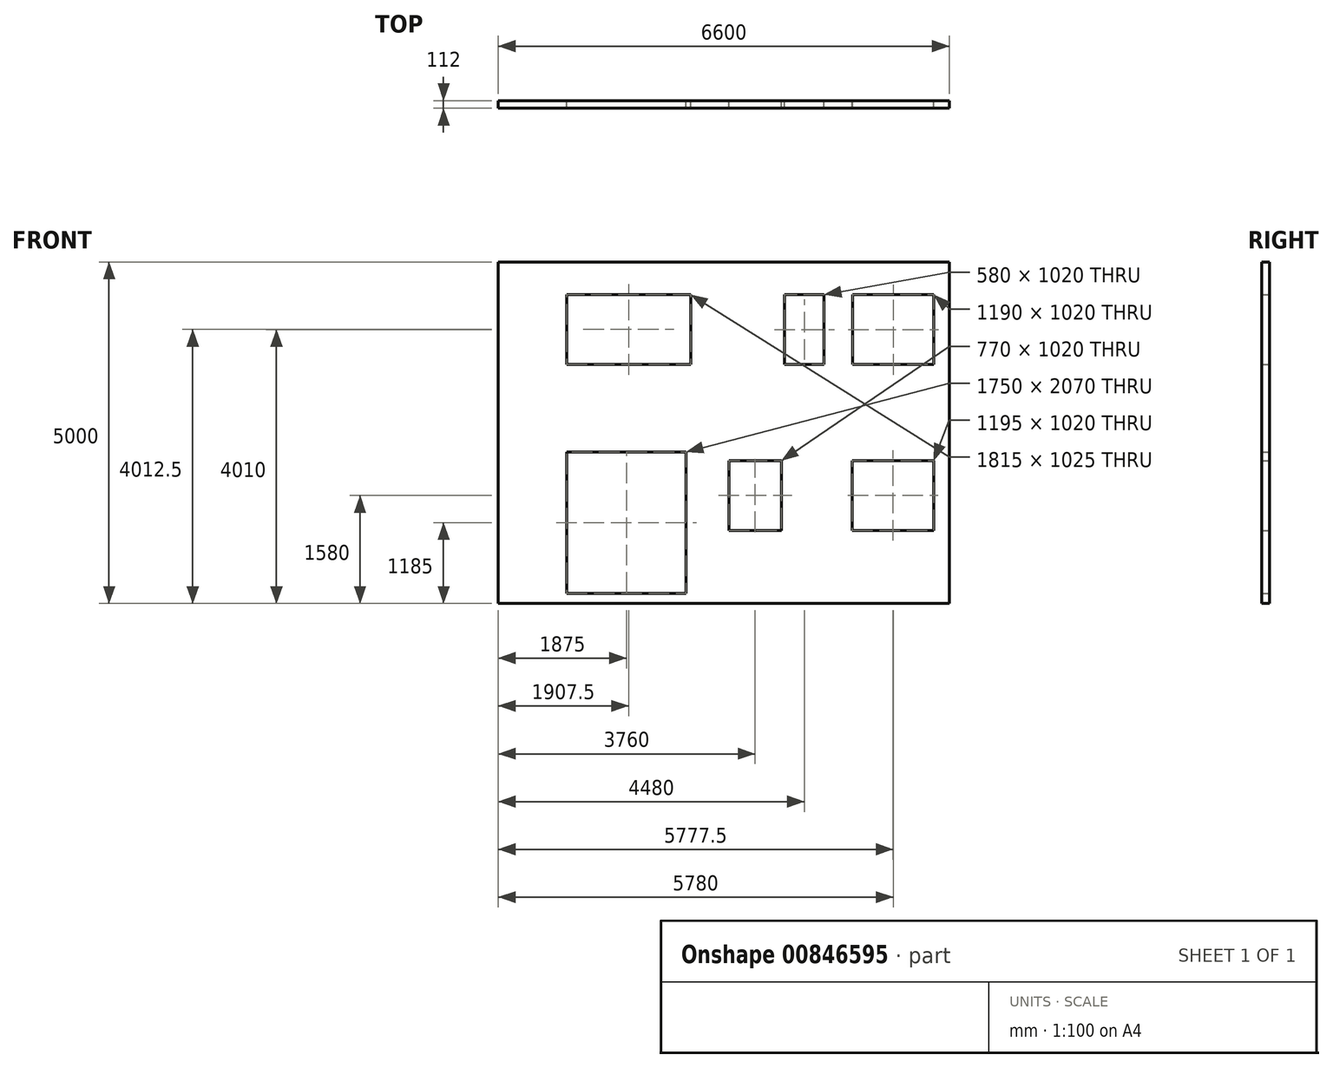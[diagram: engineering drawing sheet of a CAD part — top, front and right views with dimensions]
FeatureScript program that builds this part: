
annotation { "Feature Type Name" : "Feature", "Feature Type Description" : "" }
export const myFeature = defineFeature(function(context is Context, id is Id, definition is map)
    precondition{}
    {
        {
            var Q0;
            Q0=qCreatedBy(makeId("Front.planeOp"),FACE);
            var sketch = newSketch(context, id + "F0", { "sketchPlane" : qUnion([Q0])});
            skLineSegment(sketch, "E0.bottom", {"start": v(3288.8, -2773.48) * mm, "end": v(-3311.2, -2773.48) * mm});
            skLineSegment(sketch, "E0.top", {"start": v(3288.8, 2226.52) * mm, "end": v(-3311.2, 2226.52) * mm});
            skLineSegment(sketch, "E0.left", {"start": v(3288.8, -2773.48) * mm, "end": v(3288.8, 2226.52) * mm});
            skLineSegment(sketch, "E0.right", {"start": v(-3311.2, -2773.48) * mm, "end": v(-3311.2, 2226.52) * mm});
            skLineSegment(sketch, "E1.bottom", {"start": v(-2311.2, 1751.52) * mm, "end": v(-496.2, 1751.52) * mm});
            skLineSegment(sketch, "E1.top", {"start": v(-2311.2, 726.52) * mm, "end": v(-496.2, 726.52) * mm});
            skLineSegment(sketch, "E1.left", {"start": v(-2311.2, 1751.52) * mm, "end": v(-2311.2, 726.52) * mm});
            skLineSegment(sketch, "E1.right", {"start": v(-496.2, 1751.52) * mm, "end": v(-496.2, 726.52) * mm});
            skLineSegment(sketch, "E2.bottom", {"start": v(1458.8, 1746.52) * mm, "end": v(878.8, 1746.52) * mm});
            skLineSegment(sketch, "E2.top", {"start": v(1458.8, 726.52) * mm, "end": v(878.8, 726.52) * mm});
            skLineSegment(sketch, "E2.left", {"start": v(1458.8, 1746.52) * mm, "end": v(1458.8, 726.52) * mm});
            skLineSegment(sketch, "E2.right", {"start": v(878.8, 1746.52) * mm, "end": v(878.8, 726.52) * mm});
            skLineSegment(sketch, "E3.bottom", {"start": v(3063.8, 1746.52) * mm, "end": v(1873.8, 1746.52) * mm});
            skLineSegment(sketch, "E3.top", {"start": v(3063.8, 726.52) * mm, "end": v(1873.8, 726.52) * mm});
            skLineSegment(sketch, "E3.left", {"start": v(3063.8, 1746.52) * mm, "end": v(3063.8, 726.52) * mm});
            skLineSegment(sketch, "E3.right", {"start": v(1873.8, 1746.52) * mm, "end": v(1873.8, 726.52) * mm});
            skLineSegment(sketch, "E4.bottom", {"start": v(3063.8, -1703.48) * mm, "end": v(1868.8, -1703.48) * mm});
            skLineSegment(sketch, "E4.top", {"start": v(3063.8, -683.48) * mm, "end": v(1868.8, -683.48) * mm});
            skLineSegment(sketch, "E4.left", {"start": v(3063.8, -1703.48) * mm, "end": v(3063.8, -683.48) * mm});
            skLineSegment(sketch, "E4.right", {"start": v(1868.8, -1703.48) * mm, "end": v(1868.8, -683.48) * mm});
            skLineSegment(sketch, "E5.bottom", {"start": v(833.8, -683.48) * mm, "end": v(63.8, -683.48) * mm});
            skLineSegment(sketch, "E5.top", {"start": v(833.8, -1703.48) * mm, "end": v(63.8, -1703.48) * mm});
            skLineSegment(sketch, "E5.left", {"start": v(833.8, -683.48) * mm, "end": v(833.8, -1703.48) * mm});
            skLineSegment(sketch, "E5.right", {"start": v(63.8, -683.48) * mm, "end": v(63.8, -1703.48) * mm});
            skLineSegment(sketch, "E6.bottom", {"start": v(-561.2, -553.48) * mm, "end": v(-2311.2, -553.48) * mm});
            skLineSegment(sketch, "E6.top", {"start": v(-561.2, -2623.48) * mm, "end": v(-2311.2, -2623.48) * mm});
            skLineSegment(sketch, "E6.left", {"start": v(-561.2, -553.48) * mm, "end": v(-561.2, -2623.48) * mm});
            skLineSegment(sketch, "E6.right", {"start": v(-2311.2, -553.48) * mm, "end": v(-2311.2, -2623.48) * mm});
            skSolve(sketch);
        }
        {
            var Q0;
            Q0=qSketchRegion(id+"F0",true);
            extrude(context, id + "F1", {"entities" : qUnion([Q0]), "depth" : 112 * mm, "offsetDistance" : 25 * mm});
        }
    });
